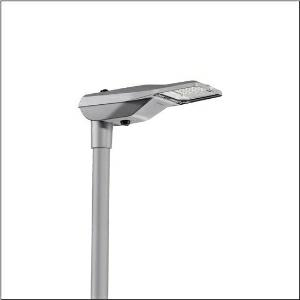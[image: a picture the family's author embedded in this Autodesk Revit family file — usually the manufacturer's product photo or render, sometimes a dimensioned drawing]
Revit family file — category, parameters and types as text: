
# Revit family: streetlight_sl_21_iq_micro___p0_5a_5xe1v31y08cb_657a
name_source: partatom
category: Lighting Fixtures
units: mm (PartAtom-declared; Revit-internal decimal feet)

## family parameters
Cut with Voids When Loaded = No
Host = Face
Light Source = No
Part Type = Normal
Room Calculation Point = No
Round Connector Dimension = Use Diameter
Shared = No

## types (1)
- --- (1 x LED, 2840 lm, 19.1 W, 3000K)
    Apparent Load = 19 VA
    CIE Flux Codes = 37 73 96 100 100
    Color Rendering = 70
    Color Temperature = 3000K
    Default Elevation = 1800 mm
    Description = Streetlight SL 21 iQ micro, mast luminaire, primary light control with lens, of PMMA, primary optical cover: cover, of toughened safety glass, transparent, light distribution: P0.5a, light emission: direct distribution, primary light characteristic: asymmetric, installation type: post-top, side-entry, LED, High Power LED, rated luminous flux: 2.840lm, luminous efficacy: 149lm/W, light colour: 730, colour temperature: 3000K, control gear: iQ-Street Remote, D4i with power reduction, control: pre-setting: logarithmic dimming characteristic, Street-Remote, Auto-Match, Temp-Guard, Lumen-Switch, Night-Set, Smart-Wire, Light-Fading, Desk-Remote (wireless, voltage-free reading and setting of iQ features in the workshop via application-optimized NFC function/RFID function), optimised constant luminous flux control (CLO 2.0), mains connection: 220..240V, AC, 50/60Hz, start of lifetime: 19W, end of service life: 20W, reduction: 9W, luminaire housing, of diecast aluminium, powder-coated, Siteco® metallic grey (DB 702S), corrosivity category C5 mid according to DIN EN ISO 12944, please order mast flange separately, inclination adjustable: 0°, 5°, 10°, 15°, sealing non-destructively replaceable, multi-level sealing system, length: 528mm, width: 235mm, height: 110mm, mast flange for spigot size: 42mm (side-entry): 5XC10008XM4, 60/48mm (side-entry/post-top): 5XC10108XM2, 76/60mm (side-entry/post-top): 5XC10108XM1, mounting height: 4..8m, Smart Interface below and above, protection rating (complete): IP66, insulation class (complete): insulation class II (safety insulation), certification: CE, ENEC, ENEC+, VDE, impact resistance: IK10, permissible operating ambient temperature for outdoor applications: -40..+50°C, standard-compliant lighting for roads and squares, packaging unit: 1 piece

Light Distribution: P0.5a
    Height = 110 mm
    Lamp = 1 x LED
    Lamp Light Flux = 2840 lm
    Lamp Power = 19.1 W
    Lamp count = 1
    Length = 528 mm
    Luminous efficacy = 149 lm/W
    Manufacturer = Siteco
    ModVariant = No
    Model = 5XE1V31Y08CB
    Number of Poles = 1
    OnlyDefault = Yes
    Power Factor = 1
    Product Name = Streetlight SL 21 iQ micro | P0.5a
    Product group = mast luminaire | pylon top
    ProductGroupID = 6100
    Protection Class = Protection class II
    Protection Degree = IP 66
    RLX_Detail_Level = 1
    RLX_Emergency_Light_Flux = 0 lm
    RLX_Emergency_Type = 0
    RLX_Emergency_Type_DB = No
    RlxData = <blob elided: 97653 chars, md5=7546df66>
    Socket = socket
    Standby Power = 0 W
    System Light Flux = 2840 lm
    System Power = 19 W
    Type Comments = factory setting: luminous flux: 100 % | dim-lin: 254 | 387 mA
    Type Image = l_1007239.jpg
    URL = http://relux.com
    VarID = @adj_070180
    Voltage = 0 V
    Weight = 0.00 kg
    Width = 235 mm

## geometry (parser evidence)
native form markers: Blend x4, Sweep x9
no freeform markers — native parametric forms only
